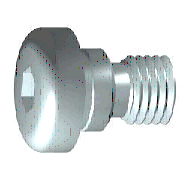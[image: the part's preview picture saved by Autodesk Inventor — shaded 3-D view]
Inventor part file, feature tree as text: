
AUTODESK INVENTOR PART (.ipt)
format: ipt  version: 2012 (Build 160160000, 160)  size: 187,904 bytes
history: native  units: mm (DEFAULTED — no unit token found)
features: other x2, extrude x1
ambient origin geometry x7: Origin, YZ Plane, XZ Plane, X Axis, Y Axis, Z Axis, Center Point
bodies: Solid1 (feature_tree), Body (feature_tree)
feature tree (3):
  extrude  "Slot"  Depth=9.525mm
  other  "Groove1"
  other  "Groove2"
